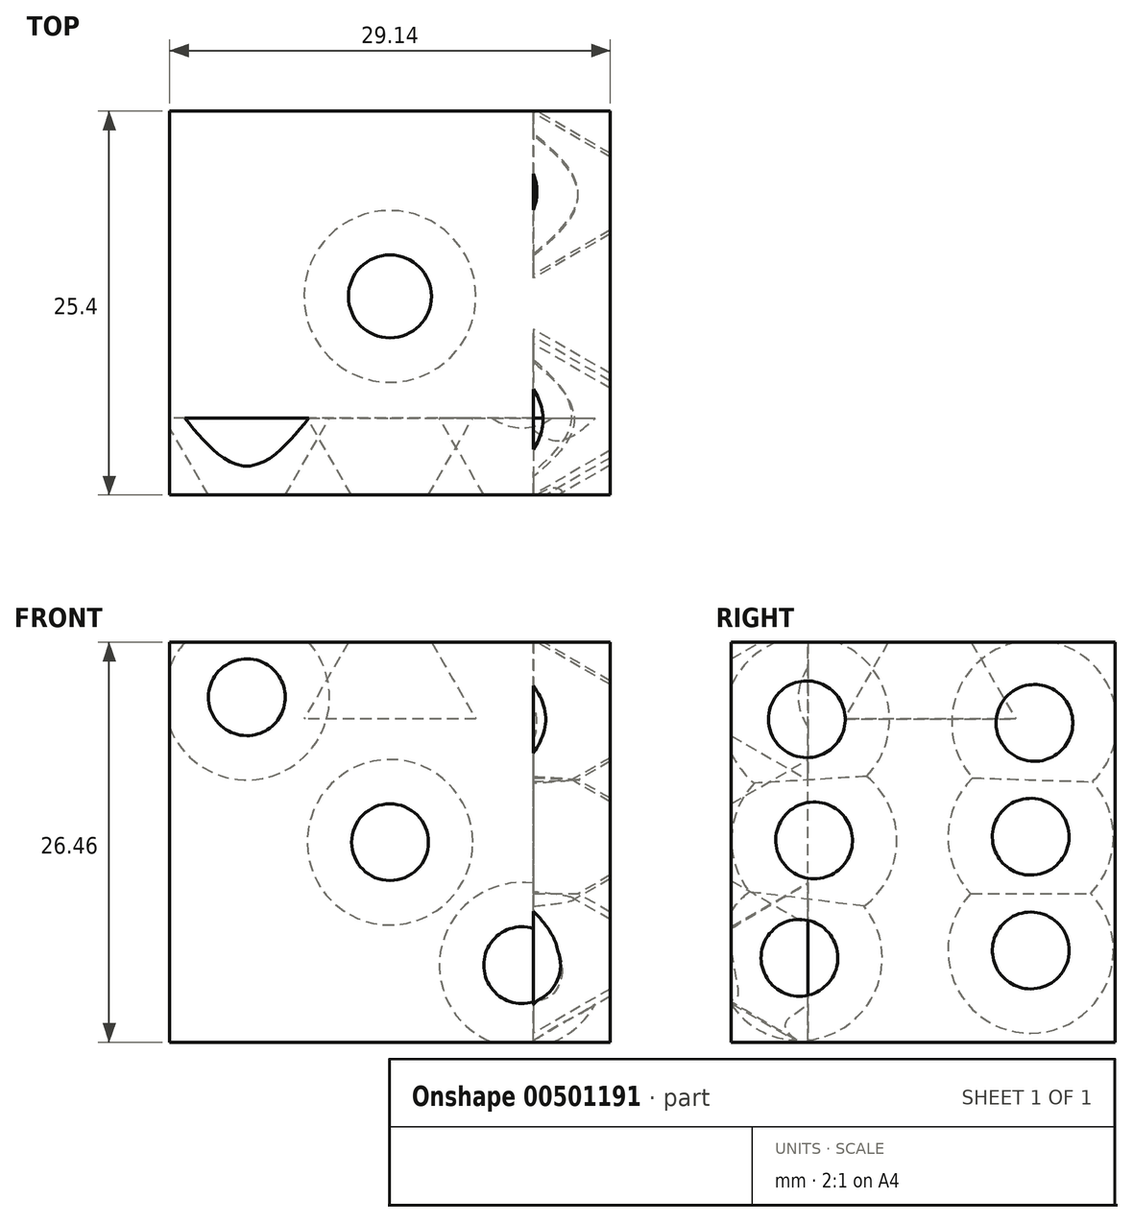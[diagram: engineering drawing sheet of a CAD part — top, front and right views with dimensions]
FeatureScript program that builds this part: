
annotation { "Feature Type Name" : "Feature", "Feature Type Description" : "" }
export const myFeature = defineFeature(function(context is Context, id is Id, definition is map)
    precondition{}
    {
        {
            var Q0;
            Q0=qCreatedBy(makeId("Front.planeOp"),FACE);
            var sketch = newSketch(context, id + "F0", { "sketchPlane" : qUnion([Q0])});
            skLineSegment(sketch, "E0.bottom", {"start": v(-14.57, 13.23) * mm, "end": v(14.57, 13.23) * mm});
            skLineSegment(sketch, "E0.top", {"start": v(-14.57, -13.23) * mm, "end": v(14.57, -13.23) * mm});
            skLineSegment(sketch, "E0.left", {"start": v(-14.57, 13.23) * mm, "end": v(-14.57, -13.23) * mm});
            skLineSegment(sketch, "E0.right", {"start": v(14.57, 13.23) * mm, "end": v(14.57, -13.23) * mm});
            skPoint(sketch, "E0.middle", {"position": v(0, 0) * mm});
            skSolve(sketch);
        }
        {
            var Q0;
            Q0=makeQuery(id+"F0.imprint","IMPRINT",FACE,{"disambiguationData":[TD([[makeQuery(id+"F0.imprint","IMPRINT",EDGE,{"derivedFrom":sQuery(id+"F0.wireOp",EDGE,"E0.bottom")}),-1.0]])]});
            extrude(context, id + "F1", {"entities" : qUnion([Q0]), "depth" : 25.4 * mm});
        }
        {
            var Q0;
            Q0=makeQuery(id+"F1.opExtrude","SWEPT_FACE",FACE,{"disambiguationData":[OSD([sQuery(id+"F0.wireOp",EDGE,"E0.bottom")])]});
            var sketch = newSketch(context, id + "F2", { "sketchPlane" : qUnion([Q0])});
            skCircle(sketch, "E1", {"center": v(0, -12.26) * mm, "radius": 2.75 * mm});
            skSolve(sketch);
        }
        {
            var Q0;
            Q0=makeQuery(id+"F2.imprint","IMPRINT",FACE,{"disambiguationData":[TD([[makeQuery(id+"F2.imprint","IMPRINT",EDGE,{"derivedFrom":sQuery(id+"F2.wireOp",EDGE,"E1")}),1.0]])]});
            extrude(context, id + "F3", {"entities" : qUnion([Q0]), "operationType" : NewBodyOperationType.REMOVE, "oppositeDirection" : true, "depth" : 5.08 * mm, "hasDraft" : true, "draftAngle" : 30 * degree});
        }
        {
            var Q0;
            Q0=makeQuery(id+"F1.opExtrude","CAP_FACE",FACE,{"disambiguationData":[OSD([sQuery(id+"F0.wireOp",EDGE,"E0.bottom"),sQuery(id+"F0.wireOp",EDGE,"E0.top"),sQuery(id+"F0.wireOp",EDGE,"E0.left"),sQuery(id+"F0.wireOp",EDGE,"E0.right")])],"isStart":false});
            var sketch = newSketch(context, id + "F4", { "sketchPlane" : qUnion([Q0])});
            skCircle(sketch, "E2", {"center": v(0, 0) * mm, "radius": 2.54 * mm});
            skCircle(sketch, "E3", {"center": v(8.74, -8.13) * mm, "radius": 2.54 * mm});
            skCircle(sketch, "E4", {"center": v(-9.47, 9.6) * mm, "radius": 2.54 * mm});
            skSolve(sketch);
        }
        {
            var Q0;
            Q0=makeQuery(id+"F4.imprint","IMPRINT",FACE,{"disambiguationData":[TD([[makeQuery(id+"F4.imprint","IMPRINT",EDGE,{"derivedFrom":sQuery(id+"F4.wireOp",EDGE,"E3")}),1.0]])]});
            var Q1;
            Q1=makeQuery(id+"F4.imprint","IMPRINT",FACE,{"disambiguationData":[TD([[makeQuery(id+"F4.imprint","IMPRINT",EDGE,{"derivedFrom":sQuery(id+"F4.wireOp",EDGE,"E2")}),1.0]])]});
            var Q2;
            Q2=makeQuery(id+"F4.imprint","IMPRINT",FACE,{"disambiguationData":[TD([[makeQuery(id+"F4.imprint","IMPRINT",EDGE,{"derivedFrom":sQuery(id+"F4.wireOp",EDGE,"E4")}),1.0]])]});
            var Q3;
            Q3=sQuery(id+"F4.wireOp",EDGE,"E4");
            var Q4;
            Q4=sQuery(id+"F4.wireOp",EDGE,"E2");
            var Q5;
            Q5=sQuery(id+"F4.wireOp",EDGE,"E3");
            extrude(context, id + "F5", {"entities" : qUnion([Q0, Q1, Q2]), "operationType" : NewBodyOperationType.REMOVE, "surfaceEntities" : qUnion([Q3, Q4, Q5]), "oppositeDirection" : true, "depth" : 5.08 * mm, "hasDraft" : true, "draftAngle" : 30 * degree});
        }
        {
            var Q0;
            Q0=makeQuery(id+"F1.opExtrude","SWEPT_FACE",FACE,{"disambiguationData":[OSD([sQuery(id+"F0.wireOp",EDGE,"E0.right")])]});
            var sketch = newSketch(context, id + "F6", { "sketchPlane" : qUnion([Q0])});
            skCircle(sketch, "E5", {"center": v(-20.4, 8.13) * mm, "radius": 2.54 * mm});
            skCircle(sketch, "E6", {"center": v(-19.91, 0.12) * mm, "radius": 2.54 * mm});
            skCircle(sketch, "E7", {"center": v(-20.88, -7.65) * mm, "radius": 2.54 * mm});
            skCircle(sketch, "E8", {"center": v(-5.34, 7.9) * mm, "radius": 2.54 * mm});
            skCircle(sketch, "E9", {"center": v(-5.58, 0.36) * mm, "radius": 2.54 * mm});
            skCircle(sketch, "E10", {"center": v(-5.58, -7.16) * mm, "radius": 2.54 * mm});
            skSolve(sketch);
        }
        {
            var Q0;
            Q0=makeQuery(id+"F6.imprint","IMPRINT",FACE,{"disambiguationData":[TD([[makeQuery(id+"F6.imprint","IMPRINT",EDGE,{"derivedFrom":sQuery(id+"F6.wireOp",EDGE,"E5")}),1.0]])]});
            var Q1;
            Q1=makeQuery(id+"F6.imprint","IMPRINT",FACE,{"disambiguationData":[TD([[makeQuery(id+"F6.imprint","IMPRINT",EDGE,{"derivedFrom":sQuery(id+"F6.wireOp",EDGE,"E6")}),1.0]])]});
            var Q2;
            Q2=makeQuery(id+"F6.imprint","IMPRINT",FACE,{"disambiguationData":[TD([[makeQuery(id+"F6.imprint","IMPRINT",EDGE,{"derivedFrom":sQuery(id+"F6.wireOp",EDGE,"E7")}),1.0]])]});
            var Q3;
            Q3=makeQuery(id+"F6.imprint","IMPRINT",FACE,{"disambiguationData":[TD([[makeQuery(id+"F6.imprint","IMPRINT",EDGE,{"derivedFrom":sQuery(id+"F6.wireOp",EDGE,"E10")}),1.0]])]});
            var Q4;
            Q4=makeQuery(id+"F6.imprint","IMPRINT",FACE,{"disambiguationData":[TD([[makeQuery(id+"F6.imprint","IMPRINT",EDGE,{"derivedFrom":sQuery(id+"F6.wireOp",EDGE,"E9")}),1.0]])]});
            var Q5;
            Q5=makeQuery(id+"F6.imprint","IMPRINT",FACE,{"disambiguationData":[TD([[makeQuery(id+"F6.imprint","IMPRINT",EDGE,{"derivedFrom":sQuery(id+"F6.wireOp",EDGE,"E8")}),1.0]])]});
            var Q6;
            Q6=sQuery(id+"F6.wireOp",EDGE,"E5");
            var Q7;
            Q7=sQuery(id+"F6.wireOp",EDGE,"E8");
            var Q8;
            Q8=sQuery(id+"F6.wireOp",EDGE,"E9");
            var Q9;
            Q9=sQuery(id+"F6.wireOp",EDGE,"E6");
            var Q10;
            Q10=sQuery(id+"F6.wireOp",EDGE,"E7");
            var Q11;
            Q11=sQuery(id+"F6.wireOp",EDGE,"E10");
            extrude(context, id + "F7", {"entities" : qUnion([Q0, Q1, Q2, Q3, Q4, Q5]), "operationType" : NewBodyOperationType.REMOVE, "surfaceEntities" : qUnion([Q6, Q7, Q8, Q9, Q10, Q11]), "oppositeDirection" : true, "depth" : 5.08 * mm, "hasDraft" : true, "draftAngle" : 30 * degree});
        }
    });
